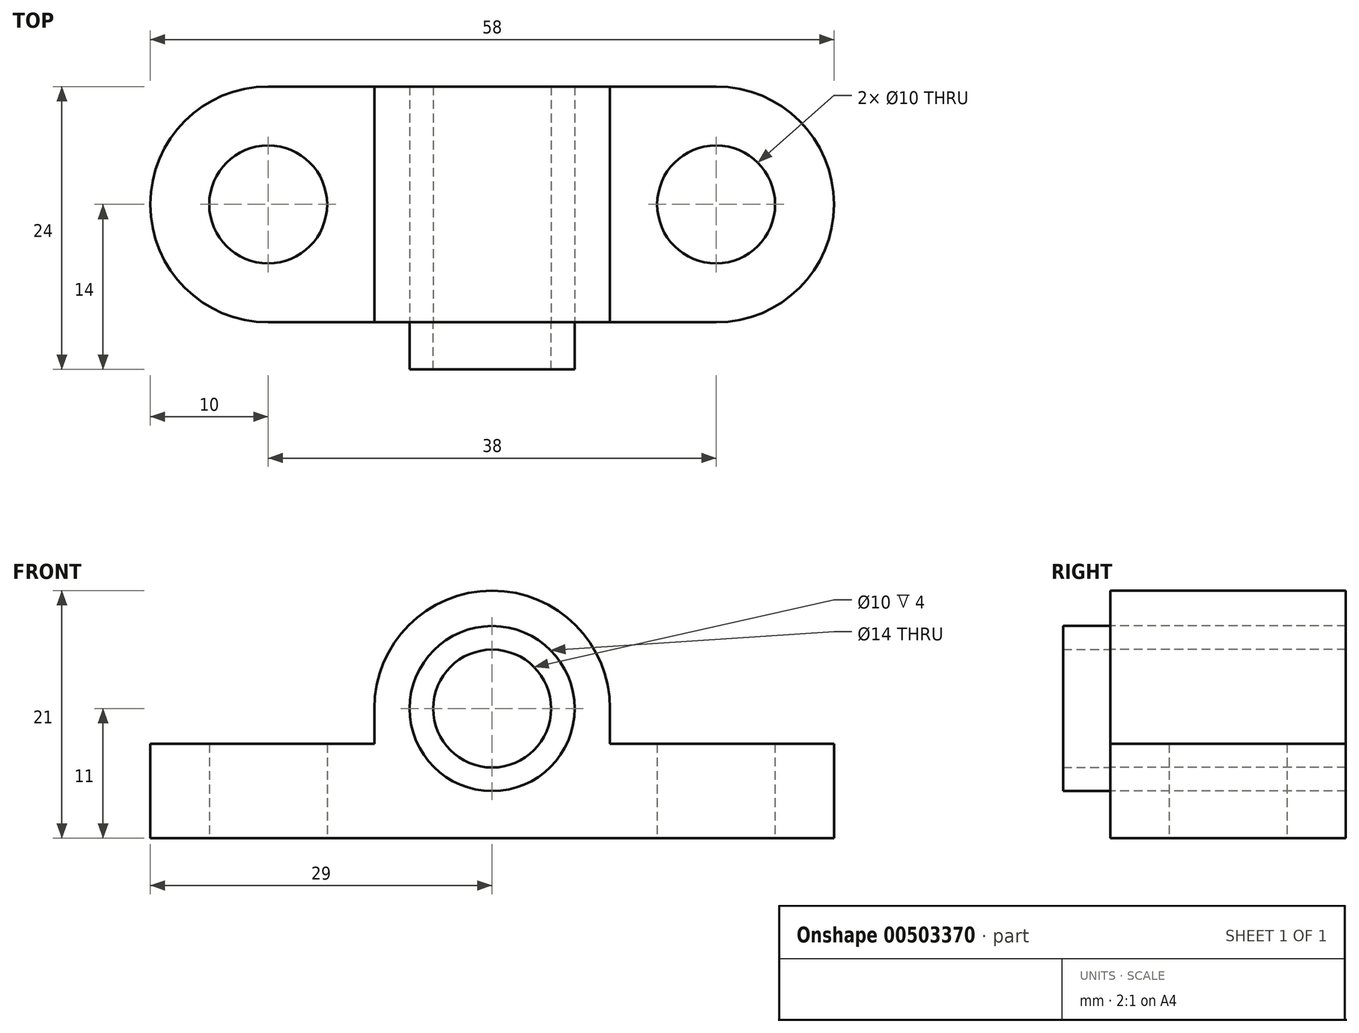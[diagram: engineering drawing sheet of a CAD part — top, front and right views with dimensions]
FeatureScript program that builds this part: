
annotation { "Feature Type Name" : "Feature", "Feature Type Description" : "" }
export const myFeature = defineFeature(function(context is Context, id is Id, definition is map)
    precondition{}
    {
        {
            var Q0;
            Q0=qCreatedBy(makeId("Top.planeOp"),FACE);
            var sketch = newSketch(context, id + "F0", { "sketchPlane" : qUnion([Q0])});
            skLineSegment(sketch, "E0.top", {"start": v(-19, -10) * mm, "end": v(19, -10) * mm});
            skPoint(sketch, "E0.middle", {"position": v(0, 0) * mm});
            skArc(sketch, "E1", {"start": v(-19, 10) * mm, "mid": v(-29, 0) * mm, "end": v(-19, -10) * mm});
            skCircle(sketch, "E2", {"center": v(-19, 0) * mm, "radius": 5 * mm});
            skArc(sketch, "E3.MirrorCS", {"start": v(19, 10) * mm, "mid": v(29, 0) * mm, "end": v(19, -10) * mm});
            skCircle(sketch, "E4.MirrorC", {"center": v(19, 0) * mm, "radius": 5 * mm});
            skLineSegment(sketch, "E5.MirrorCS", {"start": v(-19, 10) * mm, "end": v(19, 10) * mm});
            skSolve(sketch);
        }
        {
            var Q0;
            Q0 = qSketchRegion(id + "F0", true);
            extrude(context, id + "F1", {"entities" : qUnion([Q0]), "depth" : 8 * mm});
        }
        {
            var Q0;
            Q0=makeQuery(id+"F1.opExtrude","SWEPT_FACE",FACE,{"disambiguationData":[OSD([sQuery(id+"F0.wireOp",EDGE,"E0.top")])]});
            var sketch = newSketch(context, id + "F2", { "sketchPlane" : qUnion([Q0])});
            skLineSegment(sketch, "E6", {"start": v(-10, 8) * mm, "end": v(-10, 11) * mm});
            skArc(sketch, "E7", {"start": v(-10, 11) * mm, "mid": v(-7.07, 18.07) * mm, "end": v(0, 21) * mm});
            skLineSegment(sketch, "E8", {"start": v(-10, 8) * mm, "end": v(0, 8) * mm});
            skArc(sketch, "E9.MirrorCS", {"start": v(10, 11) * mm, "mid": v(7.07, 18.07) * mm, "end": v(0, 21) * mm});
            skLineSegment(sketch, "E10.MirrorCS", {"start": v(10, 8) * mm, "end": v(10, 11) * mm});
            skLineSegment(sketch, "E11.MirrorCS", {"start": v(10, 8) * mm, "end": v(0, 8) * mm});
            skSolve(sketch);
        }
        {
            var Q0;
            Q0 = qSketchRegion(id + "F2", true);
            var Q1;
            Q1=makeQuery(id+"F1.opExtrude","SWEPT_FACE",FACE,{"disambiguationData":[OSD([sQuery(id+"F0.wireOp",EDGE,"E5.MirrorCS")])]});
            extrude(context, id + "F3", {"entities" : qUnion([Q0]), "operationType" : NewBodyOperationType.ADD, "endBound" : BoundingType.UP_TO_SURFACE, "oppositeDirection" : true, "endBoundEntityFace" : qUnion([Q1]), "depth" : 25 * mm});
        }
        {
            var Q0;
            Q0=makeQuery(id+"F3.boolean.opBoolean","MERGE",FACE,{"derivedFrom":[makeQuery(id+"F1.opExtrude","SWEPT_FACE",FACE,{"disambiguationData":[OSD([sQuery(id+"F0.wireOp",EDGE,"E0.top")])]}),makeQuery(id+"F3.opExtrude","CAP_FACE",FACE,{"disambiguationData":[OSD([sQuery(id+"F2.wireOp",EDGE,"E6"),sQuery(id+"F2.wireOp",EDGE,"E7"),sQuery(id+"F2.wireOp",EDGE,"E8"),sQuery(id+"F2.wireOp",EDGE,"E9.MirrorCS"),sQuery(id+"F2.wireOp",EDGE,"E10.MirrorCS"),sQuery(id+"F2.wireOp",EDGE,"E11.MirrorCS")])],"isStart":true})]});
            var sketch = newSketch(context, id + "F4", { "sketchPlane" : qUnion([Q0])});
            skCircle(sketch, "E12", {"center": v(0, 11) * mm, "radius": 7 * mm});
            skCircle(sketch, "E13", {"center": v(0, 11) * mm, "radius": 5 * mm});
            skSolve(sketch);
        }
        {
            var Q0;
            Q0 = qSketchRegion(id + "F4", true);
            extrude(context, id + "F5", {"entities" : qUnion([Q0]), "operationType" : NewBodyOperationType.ADD, "depth" : 4 * mm});
        }
        {
            var Q0;
            Q0=makeQuery(id+"F4.imprint","IMPRINT",FACE,{"disambiguationData":[TD([[makeQuery(id+"F4.imprint","IMPRINT",EDGE,{"derivedFrom":sQuery(id+"F4.wireOp",EDGE,"E13")}),1.0]])]});
            extrude(context, id + "F6", {"entities" : qUnion([Q0]), "operationType" : NewBodyOperationType.REMOVE, "endBound" : BoundingType.THROUGH_ALL, "oppositeDirection" : true, "depth" : 25 * mm});
        }
    });
